# Revit family: Electronics_Desono_Biamp_Ultra-Compact-Passive-Subwoofer_Sublime
name_source: partatom
category: Communication Devices
units: mm (PartAtom-declared; Revit-internal decimal feet)

## family parameters
Cut with Voids When Loaded = No
Host = Face
Maintain Annotation Orientation = No
OmniClass Number = 23.85.10.11.14.14.14
OmniClass Title = Loudspeakers
Part Type = Normal
Room Calculation Point = No
Round Connector Dimension = Use Diameter
Shared = No

## types (2) — shared parameters
Connector Description = 5-way binding posts; 18V 2 x 40W 8Ω (160W peak)
Continuous Power Handling Nominal Impedance = 18V;2 x 40W @ 8Ω (160W peak)
Default Elevation = 4' - 0"
Depth = 1' - 6 1/2"
Description = Desono™ Sublime Ultra Compact Passive 6.5 Subwoofer
Environmental = IP20 per IEC 60529
Height = 1' - 4 1/2"
Input Connection = (4x) 5-way binding posts
Manufacturer = Biamp
Mounting Provisions = Wall mount bracket
Nominal Beamwidth  (H x V) = Omnidirectional
Nominal Maximum SPL @ 1m = Peak - 107dB; Continuous - 101dB
Nominal Sensitivity @ 1m = 1W - 85dB; 2.83V - 85dB
Operating Environment = Indoor
Operating Mode = Passive
Operating Range (-3dB) = 50 Hz to 200 Hz
Output Connection = (4x) 5-way binding posts
Product Documentation Link = https://downloads.biamp.com
Product Page URL = https://www.biamp.com
Product data url = https://www.bimobject.com
Protection = 3-step self-resetting protection
Recommended Amplifers = 40W - 80W @ 8Ω (19V - 27V) per input
Shipping Weight = 23.60 lb
Transducers = 1 x 6.5 (165 mm) dual voice coil (treated paper cone)
URL = https://www.biamp.com
Weight = 17.64 lb
Width = 0' - 4 1/2"

## per-type parameters (varying)
| type | Housing Material |
| SUBLIME B | Biamp - Plastic - Black |
| SUBLIME W | Biamp - Plastic - White |

note: column(s) folded — value = type name in every type: Model

## geometry (parser evidence)
native form markers: Sweep x2
no freeform markers — native parametric forms only
